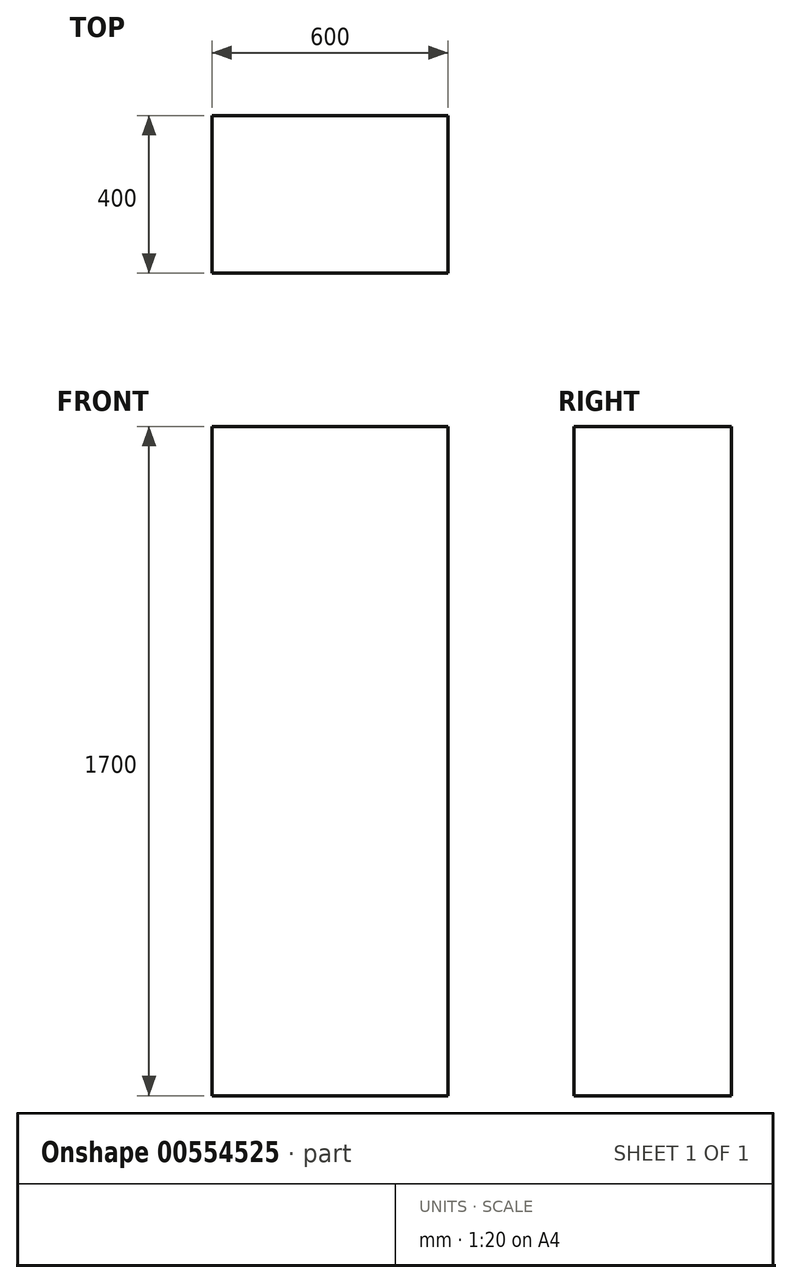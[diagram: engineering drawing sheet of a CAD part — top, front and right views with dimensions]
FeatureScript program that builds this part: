
annotation { "Feature Type Name" : "Feature", "Feature Type Description" : "" }
export const myFeature = defineFeature(function(context is Context, id is Id, definition is map)
    precondition{}
    {
        {
            var Q0;
            Q0=qCreatedBy(makeId("Top.planeOp"),FACE);
            var sketch = newSketch(context, id + "F0", { "sketchPlane" : qUnion([Q0])});
            skLineSegment(sketch, "E0.bottom", {"start": v(0, 0) * mm, "end": v(600, 0) * mm});
            skLineSegment(sketch, "E0.top", {"start": v(0, 400) * mm, "end": v(600, 400) * mm});
            skLineSegment(sketch, "E0.left", {"start": v(0, 0) * mm, "end": v(0, 400) * mm});
            skLineSegment(sketch, "E0.right", {"start": v(600, 0) * mm, "end": v(600, 400) * mm});
            skSolve(sketch);
        }
        {
            var Q0;
            Q0=makeQuery(id+"F0.imprint","IMPRINT",FACE,{"disambiguationData":[TD([[makeQuery(id+"F0.imprint","IMPRINT",EDGE,{"derivedFrom":sQuery(id+"F0.wireOp",EDGE,"E0.bottom")}),1.0]])]});
            extrude(context, id + "F1", {"entities" : qUnion([Q0]), "depth" : 1700 * mm, "offsetDistance" : 25 * mm});
        }
    });
